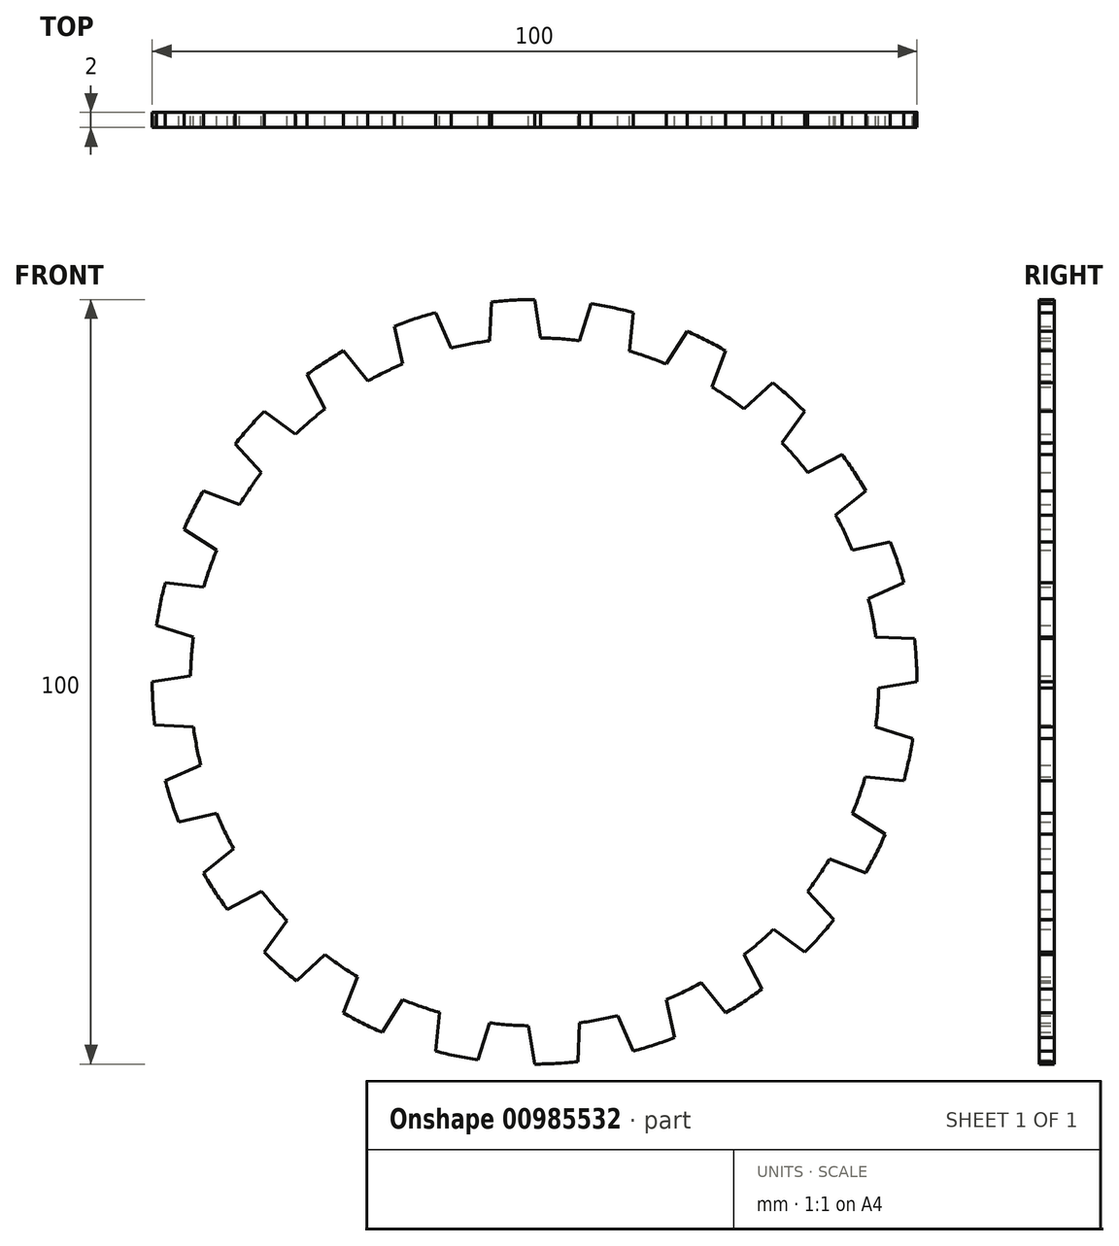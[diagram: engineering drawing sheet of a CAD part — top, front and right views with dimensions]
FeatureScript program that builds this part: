
annotation { "Feature Type Name" : "Feature", "Feature Type Description" : "" }
export const myFeature = defineFeature(function(context is Context, id is Id, definition is map)
    precondition{}
    {
        {
            var Q0;
            Q0=qCreatedBy(makeId("Front.planeOp"),FACE);
            var sketch = newSketch(context, id + "F0", { "sketchPlane" : qUnion([Q0])});
            skLineSegment(sketch, "E0", {"start": v(0, 0) * mm, "end": v(0, 50) * mm, "construction": true});
            skLineSegment(sketch, "E1", {"start": v(0, 0) * mm, "end": v(-6.53, 49.57) * mm, "construction": true});
            skLineSegment(sketch, "E2", {"start": v(0, 0) * mm, "end": v(5.87, 44.62) * mm, "construction": true});
            skLineSegment(sketch, "E3", {"start": v(0, 0) * mm, "end": v(0.87, 50) * mm, "construction": true});
            skLineSegment(sketch, "E4", {"start": v(0, 0) * mm, "end": v(-5.66, 49.68) * mm, "construction": true});
            skLineSegment(sketch, "E5", {"start": v(-5.87, 44.62) * mm, "end": v(-5.66, 49.68) * mm});
            skLineSegment(sketch, "E6", {"start": v(0, 50) * mm, "end": v(0.79, 45) * mm});
            skArc(sketch, "E7", {"start": v(-5.87, 44.62) * mm, "mid": v(0, -45) * mm, "end": v(5.87, 44.62) * mm, "construction": true});
            skArc(sketch, "E8", {"start": v(0.79, 45) * mm, "mid": v(-2.55, 44.93) * mm, "end": v(-5.87, 44.62) * mm, "construction": true});
            skLineSegment(sketch, "E9", {"start": v(5.87, 44.62) * mm, "end": v(5.87, 44.62) * mm});
            skArc(sketch, "E10", {"start": v(0, 50) * mm, "mid": v(-2.83, 49.92) * mm, "end": v(-5.66, 49.68) * mm});
            skArc(sketch, "E11", {"start": v(-5.66, 49.68) * mm, "mid": v(2.83, -49.92) * mm, "end": v(0, 50) * mm, "construction": true});
            skLineSegment(sketch, "E12", {"start": v(5.87, 44.62) * mm, "end": v(6.53, 49.57) * mm, "construction": true});
            skArc(sketch, "E13", {"start": v(5.87, 44.62) * mm, "mid": v(3.33, 44.88) * mm, "end": v(0.79, 45) * mm});
            skLineSegment(sketch, "E14.1.0", {"start": v(-17.22, 41.57) * mm, "end": v(-18.33, 46.52) * mm});
            skArc(sketch, "E14.1.1", {"start": v(-12.94, 48.3) * mm, "mid": v(-15.66, 47.48) * mm, "end": v(-18.33, 46.52) * mm});
            skLineSegment(sketch, "E14.1.2", {"start": v(-12.94, 48.3) * mm, "end": v(-10.89, 43.66) * mm});
            skArc(sketch, "E14.1.3", {"start": v(-5.87, 44.62) * mm, "mid": v(-8.4, 44.21) * mm, "end": v(-10.89, 43.66) * mm});
            skLineSegment(sketch, "E14.2.0", {"start": v(-27.4, 35.7) * mm, "end": v(-29.74, 40.2) * mm});
            skArc(sketch, "E14.2.1", {"start": v(-25, 43.3) * mm, "mid": v(-27.41, 41.81) * mm, "end": v(-29.74, 40.2) * mm});
            skLineSegment(sketch, "E14.2.2", {"start": v(-25, 43.3) * mm, "end": v(-21.82, 39.36) * mm});
            skArc(sketch, "E14.2.3", {"start": v(-17.22, 41.57) * mm, "mid": v(-19.55, 40.53) * mm, "end": v(-21.82, 39.36) * mm});
            skLineSegment(sketch, "E14.3.0", {"start": v(-35.7, 27.4) * mm, "end": v(-39.13, 31.13) * mm});
            skArc(sketch, "E14.3.1", {"start": v(-35.36, 35.36) * mm, "mid": v(-37.3, 33.3) * mm, "end": v(-39.13, 31.13) * mm});
            skLineSegment(sketch, "E14.3.2", {"start": v(-35.36, 35.36) * mm, "end": v(-31.26, 32.37) * mm});
            skArc(sketch, "E14.3.3", {"start": v(-27.4, 35.7) * mm, "mid": v(-29.37, 34.1) * mm, "end": v(-31.26, 32.37) * mm});
            skLineSegment(sketch, "E14.4.0", {"start": v(-41.57, 17.22) * mm, "end": v(-45.85, 19.94) * mm});
            skArc(sketch, "E14.4.1", {"start": v(-43.3, 25) * mm, "mid": v(-44.65, 22.5) * mm, "end": v(-45.85, 19.94) * mm});
            skLineSegment(sketch, "E14.4.2", {"start": v(-43.3, 25) * mm, "end": v(-38.57, 23.18) * mm});
            skArc(sketch, "E14.4.3", {"start": v(-35.7, 27.4) * mm, "mid": v(-37.2, 25.33) * mm, "end": v(-38.57, 23.18) * mm});
            skLineSegment(sketch, "E14.5.0", {"start": v(-44.62, 5.87) * mm, "end": v(-49.45, 7.4) * mm});
            skArc(sketch, "E14.5.1", {"start": v(-48.3, 12.94) * mm, "mid": v(-48.95, 10.18) * mm, "end": v(-49.45, 7.4) * mm});
            skLineSegment(sketch, "E14.5.2", {"start": v(-48.3, 12.94) * mm, "end": v(-43.26, 12.4) * mm});
            skArc(sketch, "E14.5.3", {"start": v(-41.57, 17.22) * mm, "mid": v(-42.48, 14.84) * mm, "end": v(-43.26, 12.4) * mm});
            skLineSegment(sketch, "E14.6.0", {"start": v(-44.62, -5.87) * mm, "end": v(-49.68, -5.66) * mm});
            skArc(sketch, "E14.6.1", {"start": v(-50, 0) * mm, "mid": v(-49.92, -2.83) * mm, "end": v(-49.68, -5.66) * mm});
            skLineSegment(sketch, "E14.6.2", {"start": v(-50, 0) * mm, "end": v(-45, 0.79) * mm});
            skArc(sketch, "E14.6.3", {"start": v(-44.62, 5.87) * mm, "mid": v(-44.88, 3.33) * mm, "end": v(-45, 0.79) * mm});
            skLineSegment(sketch, "E14.7.0", {"start": v(-41.57, -17.22) * mm, "end": v(-46.52, -18.33) * mm});
            skArc(sketch, "E14.7.1", {"start": v(-48.3, -12.94) * mm, "mid": v(-47.48, -15.66) * mm, "end": v(-46.52, -18.33) * mm});
            skLineSegment(sketch, "E14.7.2", {"start": v(-48.3, -12.94) * mm, "end": v(-43.66, -10.89) * mm});
            skArc(sketch, "E14.7.3", {"start": v(-44.62, -5.87) * mm, "mid": v(-44.21, -8.4) * mm, "end": v(-43.66, -10.89) * mm});
            skLineSegment(sketch, "E14.8.0", {"start": v(-35.7, -27.4) * mm, "end": v(-40.2, -29.74) * mm});
            skArc(sketch, "E14.8.1", {"start": v(-43.3, -25) * mm, "mid": v(-41.81, -27.41) * mm, "end": v(-40.2, -29.74) * mm});
            skLineSegment(sketch, "E14.8.2", {"start": v(-43.3, -25) * mm, "end": v(-39.36, -21.82) * mm});
            skArc(sketch, "E14.8.3", {"start": v(-41.57, -17.22) * mm, "mid": v(-40.53, -19.55) * mm, "end": v(-39.36, -21.82) * mm});
            skLineSegment(sketch, "E14.9.0", {"start": v(-27.4, -35.7) * mm, "end": v(-31.13, -39.13) * mm});
            skArc(sketch, "E14.9.1", {"start": v(-35.36, -35.36) * mm, "mid": v(-33.3, -37.3) * mm, "end": v(-31.13, -39.13) * mm});
            skLineSegment(sketch, "E14.9.2", {"start": v(-35.36, -35.36) * mm, "end": v(-32.37, -31.26) * mm});
            skArc(sketch, "E14.9.3", {"start": v(-35.7, -27.4) * mm, "mid": v(-34.1, -29.37) * mm, "end": v(-32.37, -31.26) * mm});
            skLineSegment(sketch, "E14.10.0", {"start": v(-17.22, -41.57) * mm, "end": v(-19.94, -45.85) * mm});
            skArc(sketch, "E14.10.1", {"start": v(-25, -43.3) * mm, "mid": v(-22.5, -44.65) * mm, "end": v(-19.94, -45.85) * mm});
            skLineSegment(sketch, "E14.10.2", {"start": v(-25, -43.3) * mm, "end": v(-23.18, -38.57) * mm});
            skArc(sketch, "E14.10.3", {"start": v(-27.4, -35.7) * mm, "mid": v(-25.33, -37.2) * mm, "end": v(-23.18, -38.57) * mm});
            skLineSegment(sketch, "E14.11.0", {"start": v(-5.87, -44.62) * mm, "end": v(-7.4, -49.45) * mm});
            skArc(sketch, "E14.11.1", {"start": v(-12.94, -48.3) * mm, "mid": v(-10.18, -48.95) * mm, "end": v(-7.4, -49.45) * mm});
            skLineSegment(sketch, "E14.11.2", {"start": v(-12.94, -48.3) * mm, "end": v(-12.4, -43.26) * mm});
            skArc(sketch, "E14.11.3", {"start": v(-17.22, -41.57) * mm, "mid": v(-14.84, -42.48) * mm, "end": v(-12.4, -43.26) * mm});
            skLineSegment(sketch, "E14.12.0", {"start": v(5.87, -44.62) * mm, "end": v(5.66, -49.68) * mm});
            skArc(sketch, "E14.12.1", {"start": v(0, -50) * mm, "mid": v(2.83, -49.92) * mm, "end": v(5.66, -49.68) * mm});
            skLineSegment(sketch, "E14.12.2", {"start": v(0, -50) * mm, "end": v(-0.79, -45) * mm});
            skArc(sketch, "E14.12.3", {"start": v(-5.87, -44.62) * mm, "mid": v(-3.33, -44.88) * mm, "end": v(-0.79, -45) * mm});
            skLineSegment(sketch, "E14.13.0", {"start": v(17.22, -41.57) * mm, "end": v(18.33, -46.52) * mm});
            skArc(sketch, "E14.13.1", {"start": v(12.94, -48.3) * mm, "mid": v(15.66, -47.48) * mm, "end": v(18.33, -46.52) * mm});
            skLineSegment(sketch, "E14.13.2", {"start": v(12.94, -48.3) * mm, "end": v(10.89, -43.66) * mm});
            skArc(sketch, "E14.13.3", {"start": v(5.87, -44.62) * mm, "mid": v(8.4, -44.21) * mm, "end": v(10.89, -43.66) * mm});
            skLineSegment(sketch, "E14.14.0", {"start": v(27.4, -35.7) * mm, "end": v(29.74, -40.2) * mm});
            skArc(sketch, "E14.14.1", {"start": v(25, -43.3) * mm, "mid": v(27.41, -41.81) * mm, "end": v(29.74, -40.2) * mm});
            skLineSegment(sketch, "E14.14.2", {"start": v(25, -43.3) * mm, "end": v(21.82, -39.36) * mm});
            skArc(sketch, "E14.14.3", {"start": v(17.22, -41.57) * mm, "mid": v(19.55, -40.53) * mm, "end": v(21.82, -39.36) * mm});
            skLineSegment(sketch, "E14.15.0", {"start": v(35.7, -27.4) * mm, "end": v(39.13, -31.13) * mm});
            skArc(sketch, "E14.15.1", {"start": v(35.36, -35.36) * mm, "mid": v(37.3, -33.3) * mm, "end": v(39.13, -31.13) * mm});
            skLineSegment(sketch, "E14.15.2", {"start": v(35.36, -35.36) * mm, "end": v(31.26, -32.37) * mm});
            skArc(sketch, "E14.15.3", {"start": v(27.4, -35.7) * mm, "mid": v(29.37, -34.1) * mm, "end": v(31.26, -32.37) * mm});
            skLineSegment(sketch, "E14.16.0", {"start": v(41.57, -17.22) * mm, "end": v(45.85, -19.94) * mm});
            skArc(sketch, "E14.16.1", {"start": v(43.3, -25) * mm, "mid": v(44.65, -22.5) * mm, "end": v(45.85, -19.94) * mm});
            skLineSegment(sketch, "E14.16.2", {"start": v(43.3, -25) * mm, "end": v(38.57, -23.18) * mm});
            skArc(sketch, "E14.16.3", {"start": v(35.7, -27.4) * mm, "mid": v(37.2, -25.33) * mm, "end": v(38.57, -23.18) * mm});
            skLineSegment(sketch, "E14.17.0", {"start": v(44.62, -5.87) * mm, "end": v(49.45, -7.4) * mm});
            skArc(sketch, "E14.17.1", {"start": v(48.3, -12.94) * mm, "mid": v(48.95, -10.18) * mm, "end": v(49.45, -7.4) * mm});
            skLineSegment(sketch, "E14.17.2", {"start": v(48.3, -12.94) * mm, "end": v(43.26, -12.4) * mm});
            skArc(sketch, "E14.17.3", {"start": v(41.57, -17.22) * mm, "mid": v(42.48, -14.84) * mm, "end": v(43.26, -12.4) * mm});
            skLineSegment(sketch, "E14.18.0", {"start": v(44.62, 5.87) * mm, "end": v(49.68, 5.66) * mm});
            skArc(sketch, "E14.18.1", {"start": v(50, 0) * mm, "mid": v(49.92, 2.83) * mm, "end": v(49.68, 5.66) * mm});
            skLineSegment(sketch, "E14.18.2", {"start": v(50, 0) * mm, "end": v(45, -0.79) * mm});
            skArc(sketch, "E14.18.3", {"start": v(44.62, -5.87) * mm, "mid": v(44.88, -3.33) * mm, "end": v(45, -0.79) * mm});
            skLineSegment(sketch, "E14.19.0", {"start": v(41.57, 17.22) * mm, "end": v(46.52, 18.33) * mm});
            skArc(sketch, "E14.19.1", {"start": v(48.3, 12.94) * mm, "mid": v(47.48, 15.66) * mm, "end": v(46.52, 18.33) * mm});
            skLineSegment(sketch, "E14.19.2", {"start": v(48.3, 12.94) * mm, "end": v(43.66, 10.89) * mm});
            skArc(sketch, "E14.19.3", {"start": v(44.62, 5.87) * mm, "mid": v(44.21, 8.4) * mm, "end": v(43.66, 10.89) * mm});
            skLineSegment(sketch, "E14.20.0", {"start": v(35.7, 27.4) * mm, "end": v(40.2, 29.74) * mm});
            skArc(sketch, "E14.20.1", {"start": v(43.3, 25) * mm, "mid": v(41.81, 27.41) * mm, "end": v(40.2, 29.74) * mm});
            skLineSegment(sketch, "E14.20.2", {"start": v(43.3, 25) * mm, "end": v(39.36, 21.82) * mm});
            skArc(sketch, "E14.20.3", {"start": v(41.57, 17.22) * mm, "mid": v(40.53, 19.55) * mm, "end": v(39.36, 21.82) * mm});
            skLineSegment(sketch, "E14.21.0", {"start": v(27.4, 35.7) * mm, "end": v(31.13, 39.13) * mm});
            skArc(sketch, "E14.21.1", {"start": v(35.36, 35.36) * mm, "mid": v(33.3, 37.3) * mm, "end": v(31.13, 39.13) * mm});
            skLineSegment(sketch, "E14.21.2", {"start": v(35.36, 35.36) * mm, "end": v(32.37, 31.26) * mm});
            skArc(sketch, "E14.21.3", {"start": v(35.7, 27.4) * mm, "mid": v(34.1, 29.37) * mm, "end": v(32.37, 31.26) * mm});
            skLineSegment(sketch, "E14.22.0", {"start": v(17.22, 41.57) * mm, "end": v(19.94, 45.85) * mm});
            skArc(sketch, "E14.22.1", {"start": v(25, 43.3) * mm, "mid": v(22.5, 44.65) * mm, "end": v(19.94, 45.85) * mm});
            skLineSegment(sketch, "E14.22.2", {"start": v(25, 43.3) * mm, "end": v(23.18, 38.57) * mm});
            skArc(sketch, "E14.22.3", {"start": v(27.4, 35.7) * mm, "mid": v(25.33, 37.2) * mm, "end": v(23.18, 38.57) * mm});
            skLineSegment(sketch, "E14.23.0", {"start": v(5.87, 44.62) * mm, "end": v(7.4, 49.45) * mm});
            skArc(sketch, "E14.23.1", {"start": v(12.94, 48.3) * mm, "mid": v(10.18, 48.95) * mm, "end": v(7.4, 49.45) * mm});
            skLineSegment(sketch, "E14.23.2", {"start": v(12.94, 48.3) * mm, "end": v(12.4, 43.26) * mm});
            skArc(sketch, "E14.23.3", {"start": v(17.22, 41.57) * mm, "mid": v(14.84, 42.48) * mm, "end": v(12.4, 43.26) * mm});
            skSolve(sketch);
        }
        {
            var Q0;
            Q0=makeQuery(id+"F0.imprint","IMPRINT",FACE,{"disambiguationData":[TD([[makeQuery(id+"F0.imprint","IMPRINT",EDGE,{"derivedFrom":sQuery(id+"F0.wireOp",EDGE,"E5")}),-1.0]])]});
            extrude(context, id + "F1", {"entities" : qUnion([Q0]), "depth" : 2 * mm, "offsetDistance" : 25 * mm});
        }
    });
